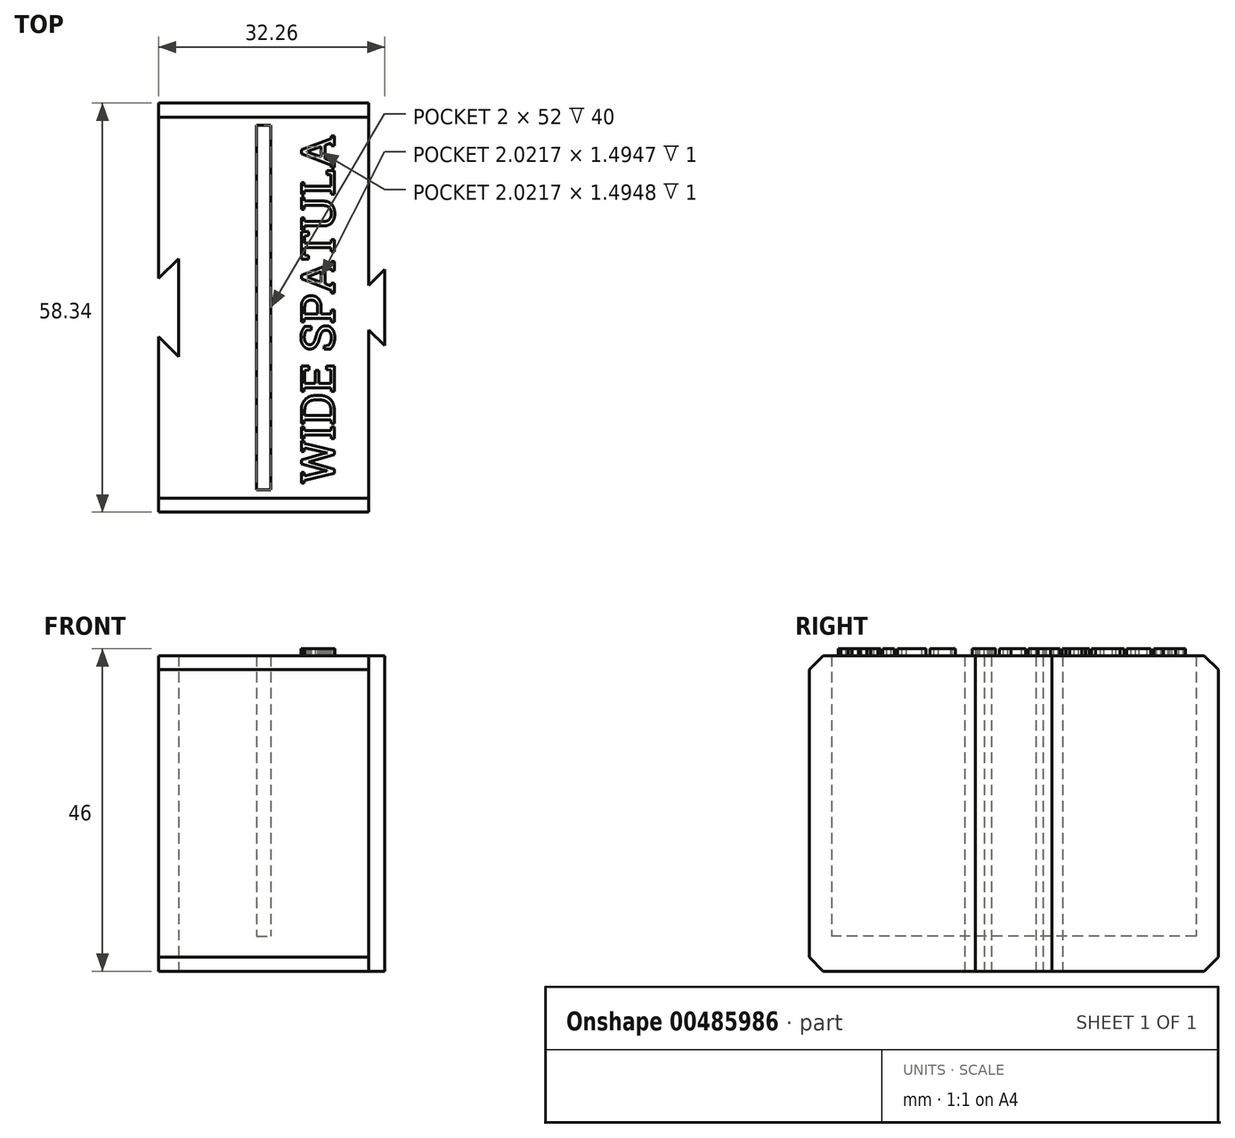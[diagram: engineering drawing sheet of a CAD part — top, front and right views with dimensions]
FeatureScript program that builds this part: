
annotation { "Feature Type Name" : "Feature", "Feature Type Description" : "" }
export const myFeature = defineFeature(function(context is Context, id is Id, definition is map)
    precondition{}
    {
        {
            var Q0;
            Q0=qCreatedBy(makeId("Top.planeOp"),FACE);
            var sketch = newSketch(context, id + "F0", { "sketchPlane" : qUnion([Q0])});
            skLineSegment(sketch, "E0", {"start": v(-15, 4.17) * mm, "end": v(-15, 29.17) * mm});
            skLineSegment(sketch, "E1", {"start": v(-15, 29.17) * mm, "end": v(15, 29.17) * mm});
            skLineSegment(sketch, "E2", {"start": v(15, 29.17) * mm, "end": v(15, 3.17) * mm});
            skLineSegment(sketch, "E3", {"start": v(-15, 4.17) * mm, "end": v(-12.17, 7) * mm});
            skLineSegment(sketch, "E4", {"start": v(-12.17, 7) * mm, "end": v(-12.17, 0) * mm});
            skLineSegment(sketch, "E5", {"start": v(15, 3.17) * mm, "end": v(17.26, 5.43) * mm});
            skLineSegment(sketch, "E6", {"start": v(17.26, 5.43) * mm, "end": v(17.26, -0.57) * mm});
            skLineSegment(sketch, "E7.MirrorCS", {"start": v(-15, -4.17) * mm, "end": v(-12.17, -7) * mm});
            skLineSegment(sketch, "E8.MirrorCS", {"start": v(15, -29.17) * mm, "end": v(15, -3.17) * mm});
            skLineSegment(sketch, "E9.MirrorCS", {"start": v(-12.17, -7) * mm, "end": v(-12.17, 0) * mm});
            skLineSegment(sketch, "E10.MirrorCS", {"start": v(-15, -4.17) * mm, "end": v(-15, -29.17) * mm});
            skLineSegment(sketch, "E11.MirrorCS", {"start": v(17.26, -5.43) * mm, "end": v(17.26, 0.57) * mm});
            skLineSegment(sketch, "E12.MirrorCS", {"start": v(15, -3.17) * mm, "end": v(17.26, -5.43) * mm});
            skLineSegment(sketch, "E13.MirrorCS", {"start": v(-15, -29.17) * mm, "end": v(15, -29.17) * mm});
            skLineSegment(sketch, "E14.bottom", {"start": v(-1, 26) * mm, "end": v(1, 26) * mm});
            skLineSegment(sketch, "E14.top", {"start": v(-1, -26) * mm, "end": v(1, -26) * mm});
            skLineSegment(sketch, "E14.left", {"start": v(-1, 26) * mm, "end": v(-1, -26) * mm});
            skLineSegment(sketch, "E14.right", {"start": v(1, 26) * mm, "end": v(1, -26) * mm});
            skPoint(sketch, "E14.middle", {"position": v(0, 0) * mm});
            skSolve(sketch);
        }
        {
            var Q0;
            Q0=qSketchRegion(id+"F0",true);
            extrude(context, id + "F1", {"entities" : qUnion([Q0]), "depth" : 40 * mm});
        }
        {
            var Q0;
            Q0=makeQuery(id+"F0.imprint","IMPRINT",FACE,{"disambiguationData":[TD([[makeQuery(id+"F0.imprint","IMPRINT",EDGE,{"derivedFrom":sQuery(id+"F0.wireOp",EDGE,"E0")}),-1.0]])]});
            var Q1;
            Q1=makeQuery(id+"F0.imprint","IMPRINT",FACE,{"disambiguationData":[TD([[makeQuery(id+"F0.imprint","IMPRINT",EDGE,{"derivedFrom":sQuery(id+"F0.wireOp",EDGE,"E14.bottom")}),-1.0]])]});
            extrude(context, id + "F2", {"entities" : qUnion([Q0, Q1]), "operationType" : NewBodyOperationType.ADD, "oppositeDirection" : true, "depth" : 5 * mm});
        }
        {
            var Q0;
            Q0=makeQuery(id+"F2.opExtrude","CAP_EDGE",EDGE,{"disambiguationData":[OSD([sQuery(id+"F0.wireOp",EDGE,"E13.MirrorCS")])],"isStart":false});
            var Q1;
            Q1=makeQuery(id+"F2.opExtrude","CAP_EDGE",EDGE,{"disambiguationData":[OSD([sQuery(id+"F0.wireOp",EDGE,"E1")])],"isStart":false});
            var Q2;
            Q2=makeQuery(id+"F1.opExtrude","CAP_EDGE",EDGE,{"disambiguationData":[OSD([sQuery(id+"F0.wireOp",EDGE,"E13.MirrorCS")])],"isStart":false});
            var Q3;
            Q3=makeQuery(id+"F1.opExtrude","CAP_EDGE",EDGE,{"disambiguationData":[OSD([sQuery(id+"F0.wireOp",EDGE,"E1")])],"isStart":false});
            chamfer(context, id + "F3", {"entities" : qUnion([Q0, Q1, Q2, Q3]), "width" : 2 * mm, "tangentPropagation" : true});
        }
        {
            var Q0;
            Q0=makeQuery(id+"F1.opExtrude","CAP_FACE",FACE,{"disambiguationData":[OSD([sQuery(id+"F0.wireOp",EDGE,"E0"),sQuery(id+"F0.wireOp",EDGE,"E1"),sQuery(id+"F0.wireOp",EDGE,"E2"),sQuery(id+"F0.wireOp",EDGE,"E3"),sQuery(id+"F0.wireOp",EDGE,"E4"),sQuery(id+"F0.wireOp",EDGE,"E5"),sQuery(id+"F0.wireOp",EDGE,"E6"),sQuery(id+"F0.wireOp",EDGE,"E7.MirrorCS"),sQuery(id+"F0.wireOp",EDGE,"E8.MirrorCS"),sQuery(id+"F0.wireOp",EDGE,"E9.MirrorCS"),sQuery(id+"F0.wireOp",EDGE,"E10.MirrorCS"),sQuery(id+"F0.wireOp",EDGE,"E11.MirrorCS"),sQuery(id+"F0.wireOp",EDGE,"E12.MirrorCS"),sQuery(id+"F0.wireOp",EDGE,"E13.MirrorCS"),sQuery(id+"F0.wireOp",EDGE,"E14.bottom"),sQuery(id+"F0.wireOp",EDGE,"E14.top"),sQuery(id+"F0.wireOp",EDGE,"E14.left"),sQuery(id+"F0.wireOp",EDGE,"E14.right")])],"isStart":false});
            var sketch = newSketch(context, id + "F4", { "sketchPlane" : qUnion([Q0])});
            skText(sketch, "E15", { "text": "WIDE SPATULA", "fontName": "RobotoSlab-Regular.ttf"});
            const initialGuessF4  = {"E15": [0.01007, -0.0251, 0, 1, 0.00477]};
            skSetInitialGuess(sketch, initialGuessF4);
            skSolve(sketch);
        }
        {
            var Q0;
            Q0=qSketchRegion(id+"F4",true);
            extrude(context, id + "F5", {"entities" : qUnion([Q0]), "operationType" : NewBodyOperationType.ADD, "depth" : 1 * mm});
        }
    });
